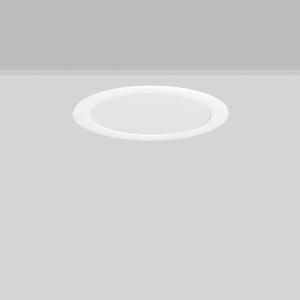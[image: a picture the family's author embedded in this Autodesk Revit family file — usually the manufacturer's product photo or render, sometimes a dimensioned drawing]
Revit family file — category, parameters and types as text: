
# Revit family: toledo_flat_round_e_672231_002_1_a98a
name_source: partatom
category: Lighting Fixtures
units: mm (PartAtom-declared; Revit-internal decimal feet)

## family parameters
Cut with Voids When Loaded = No
Host = Face
Light Source = No
Part Type = Normal
Room Calculation Point = No
Round Connector Dimension = Use Diameter
Shared = No

## types (1)
- TOLEDO FLAT round E (1 x LED Modul 840, 2250 lm, 4000)
    Apparent Load = 22 VA
    CIE Flux Codes = 49 80 96 100 100
    Color Rendering = 80
    Color Temperature = 4000
    Default Elevation = 1800 mm
    Description = Series: TOLEDO FLAT round
Ultra thin recessed downlight. For escape route illumination. Housing: die-cast aluminium, powder-coated. Lightguide and diffuser made of non-yellowing plastic (PMMA). Diffuser opal matt plastic. Ceiling installation with spring system. Including separate LED converter with connecting cable 250 mm. Suitable for connection to central battery systems. External driver with simple plug-in locking system. 
Colour: white
Diameter: 317 mm
Height: 3 mm
Cut-out diameter: 288 mm
Recess height: 35 mm
Luminaire: recess height: 31-51 mm
Weight: 1.27 kg
Operating mode: maintained power mode
Lamp: LED
Socket: without socket
Colour temperature: 4000K
Colour rendering index (CRI): 80
System power: 22 W
Rated luminous flux: 2250 lm
Luminous flux, emergency: 2250 lm
System power, emergency: 22 W
Control gear: Regulated power supply
Protection class: II
Type of protection: IP 54
    Height = 0 mm  [stored 0 ft]
    Lamp = 1 x LED Modul 840
    Lamp Light Flux = 2250 lm
    Lamp count = 1
    Length = 317 mm
    Lifetime = 50000 h
    Luminous efficacy = 102 lm/W
    Manufacturer = RZB
    ModVariant = No
    Model = 672231.002.1
    Mounting Place = Ceiling
    Mounting Type = Recessed
    Number of Poles = 1
    OnlyDefault = Yes
    Power Factor = 1
    Product Name = TOLEDO FLAT round E
    Product group = Recessed downlights
    ProductGroupID = 402
    Protection Class = Protection class II
    Protection Degree = IP 40
    RLX_Detail_Level = 1
    RLX_Emergency_Light_Flux = 2250 lm
    RLX_Emergency_Type = 3
    RLX_Emergency_Type_DB = Yes
    RlxData = <blob elided: 31333 chars, md5=1703b2a5>
    Socket = socket
    Standby Power = 0 W
    System Light Flux = 2250 lm
    System Power = 22 W
    Type Comments = Product without accessories
    Type Image = 901484.002.jpg
    URL = http://relux.com
    VarID = ---
    Voltage = 230 V
    Voltage Range = 220-240 V
    Weight = 0.00 kg
    Width = 0 mm  [stored 0 ft]

note: [stored X ft] marks values corroborated as IEEE doubles in the binary element streams (Revit-internal decimal feet)

## geometry (parser evidence)
native form markers: Blend x4, Sweep x12
no freeform markers — native parametric forms only
